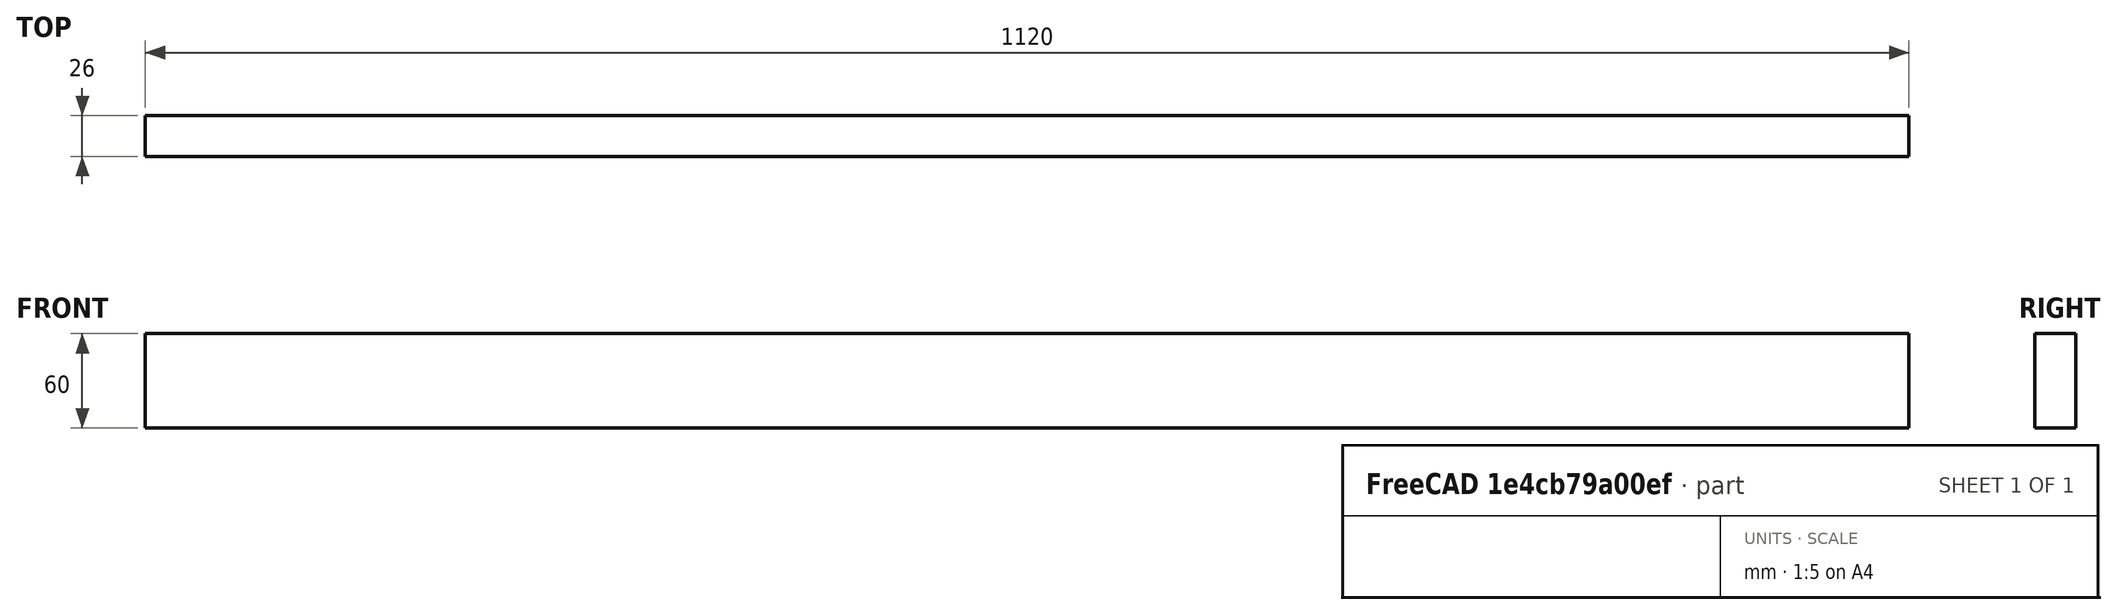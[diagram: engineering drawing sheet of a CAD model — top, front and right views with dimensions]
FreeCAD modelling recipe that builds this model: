
FCSTD DOCUMENT  (FreeCAD 0.20R29603 (Git))
Label: PanneauArrièreStand
License: All rights reserved
LicenseURL: http://en.wikipedia.org/wiki/All_rights_reserved
objects: Drawing::FeatureViewPython×4, Drawing::FeatureViewPart×3, Part::Box×1, Drawing::FeaturePage×1
note: 1 computed .brp shape members not serialized (recipe doc carries the construction recipe); baked Part::Feature solids carry a one-line shape summary decoded from their .brp

FEATURE [Part::Box] Box  label="Cube"
  AttacherType = Attacher::AttachEngine3D
  Height = 60
  Length = 1120
  Width = 26
FEATURE [Drawing::FeatureViewPart] Ortho  label="Ortho_0_0"
  Direction = (0,0,1)
  HiddenWidth = 0.15
  LineWidth = 0.35
  Rotation = 0
  Scale = 0.16
  ShowHiddenLines = false
  ShowSmoothLines = false
  Source = -> Box
  Tolerance = 0.05
  ViewResult = <g id="Ortho_0_0"\n   transform="rotate(0,33.5667,115.668) translate(33.5667,115.668) scale(0.16,0.16)"\n  >\n<g   fill="none"\n   stroke="rgb(0, 0, 0)"\n   stroke-linecap="butt"\n   stroke-linejoin="miter"\n   stroke-width="2.187500"\n   transform="scale(1,-1)"\n  >\n<path id= "1" d=" M 0 0 L 0 26 " />\n<path id= "2" d=" M 1120 0 L 1120 26 " />\n<path id= "3" d=" M 0 0 L 1120 0 " />\n<path id= "4" d=" M 0 26 L 1120 26 " />\n</g>\n</g>
  Visible = false
  X = 33.5667
  Y = 115.668
FEATURE [Drawing::FeatureViewPart] Ortho001  label="Ortho_1_0"
  Direction = (-1,0,0)
  HiddenWidth = 0.15
  LineWidth = 0.35
  Rotation = 180
  Scale = 0.16
  ShowHiddenLines = false
  ShowSmoothLines = false
  Source = -> Box
  Tolerance = 0.05
  ViewResult = <g id="Ortho_1_0"\n   transform="rotate(180,235.283,115.668) translate(235.283,115.668) scale(0.16,0.16)"\n  >\n<g   fill="none"\n   stroke="rgb(0, 0, 0)"\n   stroke-linecap="butt"\n   stroke-linejoin="miter"\n   stroke-width="2.187500"\n   transform="scale(1,-1)"\n  >\n<path id= "1" d=" M 0 0 L -60 0 " />\n<path id= "2" d=" M -60 0 L -60 -26 " />\n<path id= "3" d=" M 0 -26 L -60 -26 " />\n<path id= "4" d=" M 0 0 L 0 -26 " />\n</g>\n</g>
  Visible = false
  X = 235.283
  Y = 115.668
FEATURE [Drawing::FeatureViewPart] Ortho002  label="Ortho_0_1"
  Direction = (0,-1,0)
  HiddenWidth = 0.15
  LineWidth = 0.35
  Rotation = 90
  Scale = 0.16
  ShowHiddenLines = false
  ShowSmoothLines = false
  Source = -> Box
  Tolerance = 0.05
  ViewResult = <g id="Ortho_0_1"\n   transform="rotate(90,33.5667,65.425) translate(33.5667,65.425) scale(0.16,0.16)"\n  >\n<g   fill="none"\n   stroke="rgb(0, 0, 0)"\n   stroke-linecap="butt"\n   stroke-linejoin="miter"\n   stroke-width="2.187500"\n   transform="scale(1,-1)"\n  >\n<path id= "1" d=" M 0 0 L -60 0 " />\n<path id= "2" d=" M 0 1120 L -60 1120 " />\n<path id= "3" d=" M 0 0 L 0 1120 " />\n<path id= "4" d=" M -60 0 L -60 1120 " />\n</g>\n</g>
  Visible = false
  X = 33.5667
  Y = 65.425
FEATURE [Drawing::FeatureViewPython] dim001  # drawing view (typed FeaturePython)
  Rotation = 0
  ViewResult = <g> \n  <line x1="33.566700" y1="53.825000" x2="33.566700" y2="39.000000" style="stroke:rgb(0,0,255);stroke-width:0.30" />\n<line x1="212.766700" y1="53.825000" x2="212.766700" y2="39.000000" style="stroke:rgb(0,0,255);stroke-width:0.30" />\n<line x1="33.566700" y1="40.000000" x2="212.766700" y2="40.000000" style="stroke:rgb(0,0,255);stroke-width:0.30" /> \n  <polygon points="212.766700,40.000000 209.766700,39.000000 208.766700,40.000000 209.766700,41.000000" style="fill:rgb(0,0,255);stroke:rgb(0,0,255);stroke-width:0" /><polygon points="33.566700,40.000000 36.566700,41.000000 37.566700,40.000000 36.566700,39.000000" style="fill:rgb(0,0,255);stroke:rgb(0,0,255);stroke-width:0" /> \n  <text x="123.166700" y="38.000000" font-family="Verdana" font-size="3.6" fill="rgb(0,0,255)" text-anchor="middle" transform="rotate(0.000000 123.166700,38.000000)" >1120</text> </g>
  Visible = true
  X = 0
  Y = 0
  arrowL1 = 3
  arrowL2 = 1
  arrowW = 2
  arrow_scheme = 0
  autoPlaceOffset = 2
  autoPlaceText = true
  click1_x = 130
  click1_y = 40
  click2_x = 130
  click2_y = 40
  comma_decimal_place = false
  dimension_line_overshoot = 1
  gap_datum_points = 2
  halfDimension_linear = false
  lineColor = rgb(0,0,255)
  strokeWidth = 0.3
  textFormat_linear = %(value)3.0f
  textRenderer_color = rgb(0,0,255)
  textRenderer_family = Verdana
  textRenderer_size = 3.6
  unit_custom_scale = 1
  unit_scheme = 0
FEATURE [Drawing::FeatureViewPython] dim002  # drawing view (typed FeaturePython)
  Rotation = 0
  ViewResult = <g> \n  <line x1="214.766700" y1="65.425000" x2="241.000000" y2="65.425000" style="stroke:rgb(0,0,255);stroke-width:0.30" />\n<line x1="214.766700" y1="55.825000" x2="241.000000" y2="55.825000" style="stroke:rgb(0,0,255);stroke-width:0.30" />\n<line x1="240.000000" y1="65.425000" x2="240.000000" y2="55.825000" style="stroke:rgb(0,0,255);stroke-width:0.30" /> \n  <polygon points="240.000000,55.825000 241.000000,52.825000 240.000000,51.825000 239.000000,52.825000" style="fill:rgb(0,0,255);stroke:rgb(0,0,255);stroke-width:0" /><polygon points="240.000000,65.425000 239.000000,68.425000 240.000000,69.425000 241.000000,68.425000" style="fill:rgb(0,0,255);stroke:rgb(0,0,255);stroke-width:0" /> \n  <text x="238.000000" y="60.625000" font-family="Verdana" font-size="3.6" fill="rgb(0,0,255)" text-anchor="middle" transform="rotate(-90.000000 238.000000,60.625000)" > 60</text> </g>
  Visible = true
  X = 0
  Y = 0
  arrowL1 = 3
  arrowL2 = 1
  arrowW = 2
  arrow_scheme = 0
  autoPlaceOffset = 2
  autoPlaceText = true
  click1_x = 240
  click1_y = 60
  click2_x = 240
  click2_y = 60
  comma_decimal_place = false
  dimension_line_overshoot = 1
  gap_datum_points = 2
  halfDimension_linear = false
  lineColor = rgb(0,0,255)
  strokeWidth = 0.3
  textFormat_linear = %(value)3.0f
  textRenderer_color = rgb(0,0,255)
  textRenderer_family = Verdana
  textRenderer_size = 3.6
  unit_custom_scale = 1
  unit_scheme = 0
FEATURE [Drawing::FeatureViewPython] dim003  # drawing view (typed FeaturePython)
  Rotation = 0
  ViewResult = <g> \n  <line x1="235.283000" y1="108.708000" x2="235.283000" y2="99.000000" style="stroke:rgb(0,0,255);stroke-width:0.30" />\n<line x1="244.883000" y1="108.708000" x2="244.883000" y2="99.000000" style="stroke:rgb(0,0,255);stroke-width:0.30" />\n<line x1="235.283000" y1="100.000000" x2="244.883000" y2="100.000000" style="stroke:rgb(0,0,255);stroke-width:0.30" /> \n  <polygon points="244.883000,100.000000 247.883000,101.000000 248.883000,100.000000 247.883000,99.000000" style="fill:rgb(0,0,255);stroke:rgb(0,0,255);stroke-width:0" /><polygon points="235.283000,100.000000 232.283000,99.000000 231.283000,100.000000 232.283000,101.000000" style="fill:rgb(0,0,255);stroke:rgb(0,0,255);stroke-width:0" /> \n  <text x="240.083000" y="98.000000" font-family="Verdana" font-size="3.6" fill="rgb(0,0,255)" text-anchor="middle" transform="rotate(0.000000 240.083000,98.000000)" > 60</text> </g>
  Visible = true
  X = 0
  Y = 0
  arrowL1 = 3
  arrowL2 = 1
  arrowW = 2
  arrow_scheme = 0
  autoPlaceOffset = 2
  autoPlaceText = true
  click1_x = 240
  click1_y = 100
  click2_x = 240
  click2_y = 100
  comma_decimal_place = false
  dimension_line_overshoot = 1
  gap_datum_points = 2
  halfDimension_linear = false
  lineColor = rgb(0,0,255)
  strokeWidth = 0.3
  textFormat_linear = %(value)3.0f
  textRenderer_color = rgb(0,0,255)
  textRenderer_family = Verdana
  textRenderer_size = 3.6
  unit_custom_scale = 1
  unit_scheme = 0
FEATURE [Drawing::FeatureViewPython] dim004  # drawing view (typed FeaturePython)
  Rotation = 0
  ViewResult = <g> \n  <line x1="246.883000" y1="115.668000" x2="261.000000" y2="115.668000" style="stroke:rgb(0,0,255);stroke-width:0.30" />\n<line x1="246.883000" y1="110.708000" x2="261.000000" y2="110.708000" style="stroke:rgb(0,0,255);stroke-width:0.30" />\n<line x1="260.000000" y1="115.668000" x2="260.000000" y2="110.708000" style="stroke:rgb(0,0,255);stroke-width:0.30" /> \n  <polygon points="260.000000,110.708000 261.000000,107.708000 260.000000,106.708000 259.000000,107.708000" style="fill:rgb(0,0,255);stroke:rgb(0,0,255);stroke-width:0" /><polygon points="260.000000,115.668000 259.000000,118.668000 260.000000,119.668000 261.000000,118.668000" style="fill:rgb(0,0,255);stroke:rgb(0,0,255);stroke-width:0" /> \n  <text x="258.000000" y="113.188000" font-family="Verdana" font-size="3.6" fill="rgb(0,0,255)" text-anchor="middle" transform="rotate(-90.000000 258.000000,113.188000)" > 31</text> </g>
  Visible = true
  X = 0
  Y = 0
  arrowL1 = 3
  arrowL2 = 1
  arrowW = 2
  arrow_scheme = 0
  autoPlaceOffset = 2
  autoPlaceText = true
  click1_x = 260
  click1_y = 110
  click2_x = 260
  click2_y = 110
  comma_decimal_place = false
  dimension_line_overshoot = 1
  gap_datum_points = 2
  halfDimension_linear = false
  lineColor = rgb(0,0,255)
  strokeWidth = 0.3
  textFormat_linear = %(value)3.0f
  textRenderer_color = rgb(0,0,255)
  textRenderer_family = Verdana
  textRenderer_size = 3.6
  unit_custom_scale = 1
  unit_scheme = 0
FEATURE [Drawing::FeaturePage] Page
  EditableTexts = GB | Raidisseur haut stand | 2 exemplaires | A4 | X / Y | SCALE | PN | DN | DD/MM/YYYY | REV A
  Group = -> [Ortho,Ortho001,Ortho002,dim001,dim002,dim003,dim004]
  Template = <path>
note: 1 file-system path scrubbed to <path> (originals preserved in the JSON sidecar)
